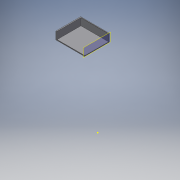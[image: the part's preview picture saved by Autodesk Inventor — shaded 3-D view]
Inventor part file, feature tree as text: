
AUTODESK INVENTOR PART (.ipt)
format: ipt  version: 2016 SP2 (Build 200236200, 236)  size: 105,472 bytes
history: native  units: mm
features: other x3, sketch x2, plane x1
ambient origin geometry x8: Origin, YZ Plane, XZ Plane, XY Plane, X Axis, Y Axis, Z Axis, Center Point
bodies: Volumenkörper1 (feature_tree)
feature tree (6):
  other  "BatCap.ipt"
  other  "Volumenkörper1::BatCap.ipt"
  other  "Bezeichnung1"
  sketch  "Skizze1"  dims[d0=10.0mm]
  sketch  "Skizze3"
  plane  "Arbeitsebene1"
